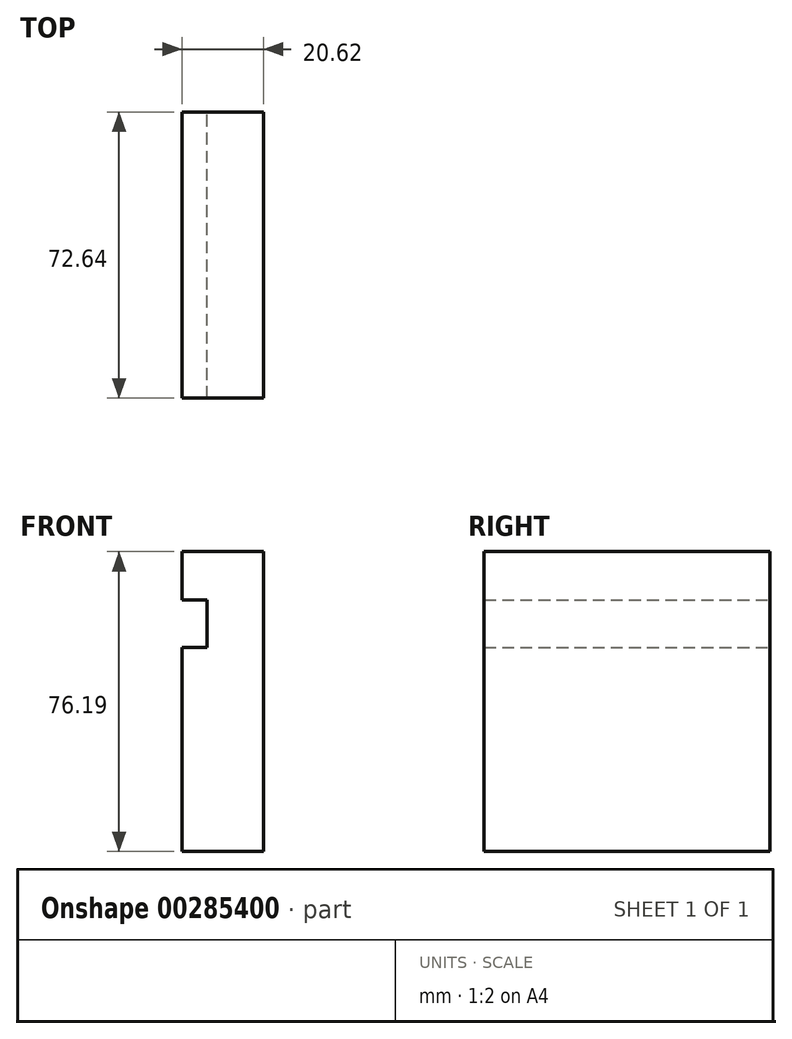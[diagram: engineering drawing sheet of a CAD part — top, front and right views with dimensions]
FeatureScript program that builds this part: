
annotation { "Feature Type Name" : "Feature", "Feature Type Description" : "" }
export const myFeature = defineFeature(function(context is Context, id is Id, definition is map)
    precondition{}
    {
        {
            var Q0;
            Q0=qCreatedBy(makeId("Front.planeOp"),FACE);
            var sketch = newSketch(context, id + "F0", { "sketchPlane" : qUnion([Q0])});
            skLineSegment(sketch, "E0.bottom", {"start": v(0, 0) * mm, "end": v(-20.62, 0) * mm});
            skLineSegment(sketch, "E0.top", {"start": v(0, 76.2) * mm, "end": v(-20.62, 76.2) * mm});
            skLineSegment(sketch, "E0.left", {"start": v(0, 0) * mm, "end": v(0, 76.2) * mm});
            skLineSegment(sketch, "E0.right", {"start": v(-20.62, 0) * mm, "end": v(-20.62, 51.83) * mm});
            skLineSegment(sketch, "E1.bottom", {"start": v(-20.62, 63.9) * mm, "end": v(-14.27, 63.9) * mm});
            skLineSegment(sketch, "E1.top", {"start": v(-20.62, 51.83) * mm, "end": v(-14.27, 51.83) * mm});
            skLineSegment(sketch, "E1.right", {"start": v(-14.27, 63.9) * mm, "end": v(-14.27, 51.83) * mm});
            skLineSegment(sketch, "E2.trimOffspring", {"start": v(-20.62, 63.9) * mm, "end": v(-20.62, 76.2) * mm});
            skSolve(sketch);
        }
        {
            var Q0;
            Q0 = qSketchRegion(id + "F0", true);
            extrude(context, id + "F1", {"entities" : qUnion([Q0]), "depth" : 72.64 * mm});
        }
    });
